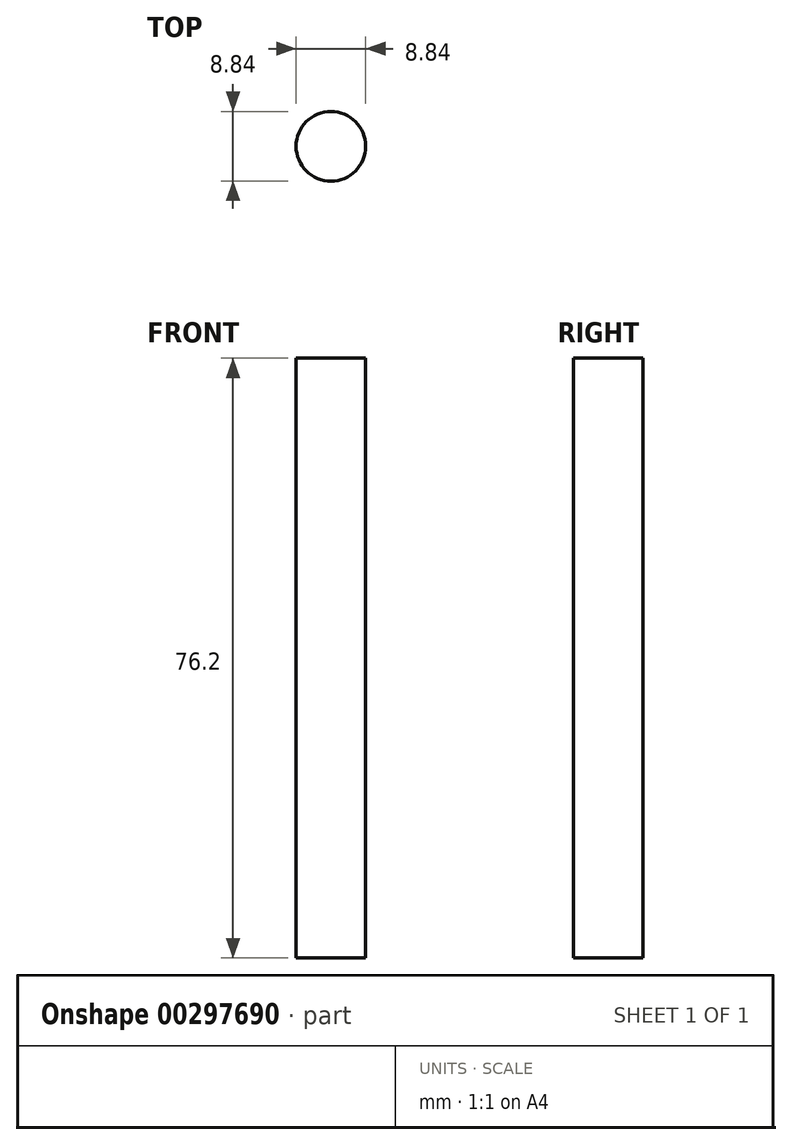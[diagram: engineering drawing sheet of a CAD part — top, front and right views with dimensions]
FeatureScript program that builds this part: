
annotation { "Feature Type Name" : "Feature", "Feature Type Description" : "" }
export const myFeature = defineFeature(function(context is Context, id is Id, definition is map)
    precondition{}
    {
        {
            var Q0;
            Q0=qCreatedBy(makeId("Front.planeOp"),FACE);
            var sketch = newSketch(context, id + "F0", { "sketchPlane" : qUnion([Q0])});
            skLineSegment(sketch, "E0", {"start": v(-16.47, 31.4) * mm, "end": v(-16.47, -44.8) * mm});
            skLineSegment(sketch, "E1", {"start": v(-7.63, 31.4) * mm, "end": v(-7.63, -44.8) * mm});
            skLineSegment(sketch, "E2", {"start": v(-16.47, 31.4) * mm, "end": v(-7.63, 31.4) * mm});
            skLineSegment(sketch, "E3", {"start": v(-7.63, -44.8) * mm, "end": v(-16.47, -44.8) * mm});
            skLineSegment(sketch, "E4", {"start": v(-12.05, 31.4) * mm, "end": v(-12.05, -44.8) * mm});
            skSolve(sketch);
        }
        {
            var Q0;
            {var subQ0=sQuery(id+"F0.wireOp",EDGE,"E1");Q0=makeQuery(id+"F0.imprint","IMPRINT",FACE,{"disambiguationData":[TD([[makeQuery(id+"F0.imprint","IMPRINT",EDGE,{"derivedFrom":subQ0}),-1.0]])]});}
            var Q1;
            Q1=sQuery(id+"F0.wireOp",EDGE,"E4");
            revolve(context, id + "F1", {"entities" : qUnion([Q0]), "axis" : qUnion([Q1]), "revolveType" : RevolveType.FULL});
        }
    });
